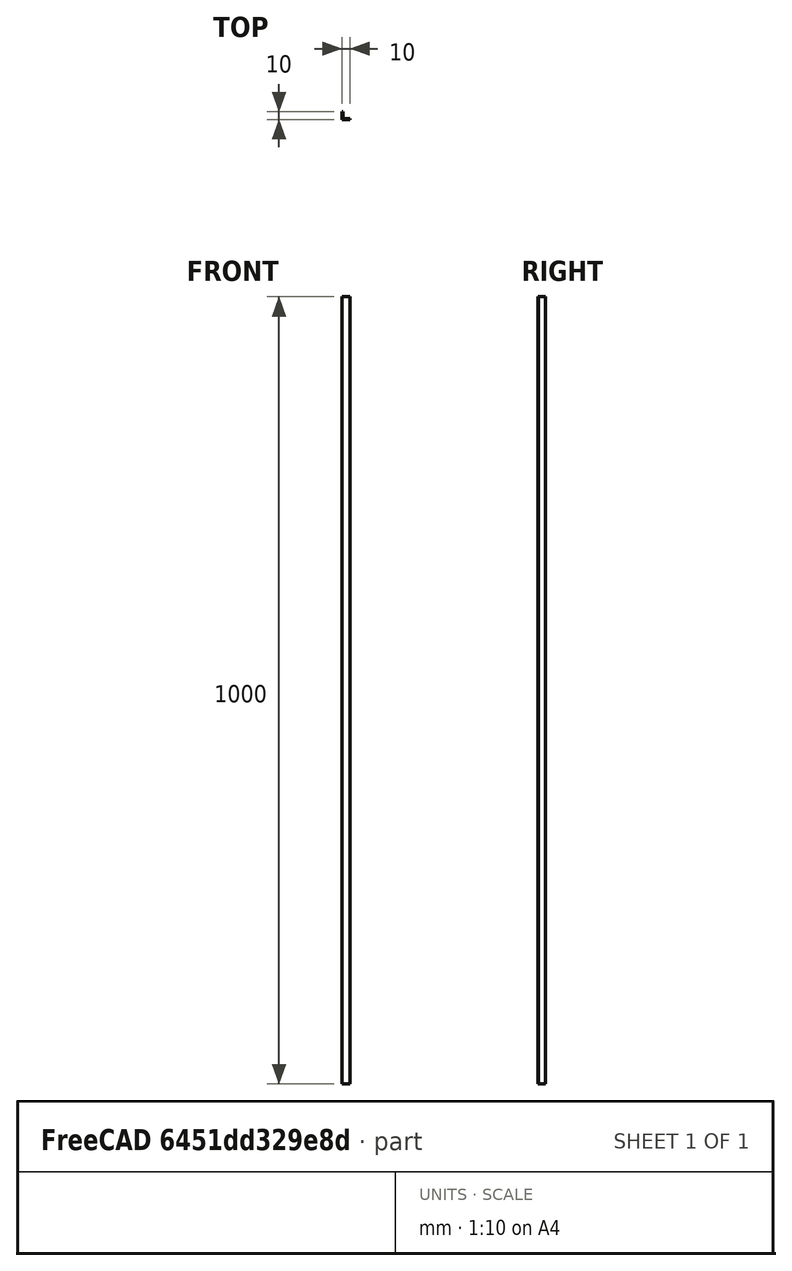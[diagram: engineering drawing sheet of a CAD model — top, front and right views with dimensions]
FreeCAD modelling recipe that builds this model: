
FCSTD DOCUMENT  (FreeCAD 0.18R16131 (Git))
Label: norm_L-profile_10_10_1
License: All rights reserved
LicenseURL: http://en.wikipedia.org/wiki/All_rights_reserved
objects: Sketcher::SketchObject×1, PartDesign::Pad×1, PartDesign::Body×1, Spreadsheet::Sheet×1
note: 4 computed .brp shape members not serialized (recipe doc carries the construction recipe); baked Part::Feature solids carry a one-line shape summary decoded from their .brp

FEATURE [Sketcher::SketchObject] Sketch
  MapMode = 5
  Support = -> [XY_Plane]
  expr: Constraints[17] = Lprofile.t1
  expr: Constraints[14] = Lprofile.d2
  expr: Constraints[16] = Lprofile.d1
  sketch-geometry (6):
    g0: LineSegment StartX=0 StartY=0 StartZ=0 EndX=0 EndY=9 EndZ=0
    g1: LineSegment StartX=0 StartY=9 StartZ=0 EndX=-1 EndY=9 EndZ=0
    g2: LineSegment StartX=-1 StartY=9 StartZ=0 EndX=-1 EndY=-1 EndZ=0
    g3: LineSegment StartX=-1 StartY=-1 StartZ=0 EndX=9 EndY=-1 EndZ=0
    g4: LineSegment StartX=9 StartY=-1 StartZ=0 EndX=9 EndY=0 EndZ=0
    g5: LineSegment StartX=9 StartY=0 StartZ=0 EndX=0 EndY=0 EndZ=0
  constraints (18):
    c: PointOnObject(g0,g-2)
    c: Vertical(g0)
    c: Coincident(g1,g0)
    c: Horizontal(g1)
    c: Coincident(g2,g1)
    c: Vertical(g2)
    c: Coincident(g3,g2)
    c: Horizontal(g3)
    c: PointOnObject(g4,g-1)
    c: Vertical(g4)
    c: Coincident(g5,g4)
    c: Coincident(g5,g0)
    c: Horizontal(g5)
    c: Equal(g1,g4)
    c: DistanceX(g3,g3) = 10
    c: Coincident(g3,g4)
    c: DistanceY(g2,g2) = 10
    c: DistanceY(g4,g4) = 1
FEATURE [PartDesign::Pad] Pad
  Length = 1000
  Length2 = 100
  Profile = -> Sketch
  Type = 0
  expr: Length = Lprofile.l1
FEATURE [PartDesign::Body] Body
  Group = -> [Sketch,Pad]
  Origin = -> Origin
  Tip = -> Pad
FEATURE [Spreadsheet::Sheet] Spreadsheet  label="Lprofile"
  cells = B3=L -Profile; B4=d1; C4(d1)=10; D4=mm; B5=d2; C5(d2)=10; D5=mm; B6=t1; C6(t1)=1; D6=mm; B7=l1; C7(l1)=1000; D7=mm
